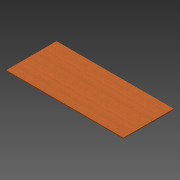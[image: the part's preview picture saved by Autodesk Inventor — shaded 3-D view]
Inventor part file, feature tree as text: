
AUTODESK INVENTOR PART (.ipt)
format: ipt  version: 2013 (Build 170138000, 138)  size: 80,896 bytes
history: native  units: in
note: dims shown in document units (in); Inventor stores cm internally (conversion verified against a paired STEP export)
features: extrude x1, sketch x1
ambient origin geometry x8: Origin, YZ Plane, XZ Plane, XY Plane, X Axis, Y Axis, Z Axis, Center Point
bodies: Solid1 (feature_tree)
feature tree (2):
  extrude  "Extrusion1"  Depth=24.0in
  sketch  "Sketch1"  dims[d0=56.0in d1=24.0in d2=0.5in d3=0.0in d4=1.213in d6=54.5in d7=0.5in]
